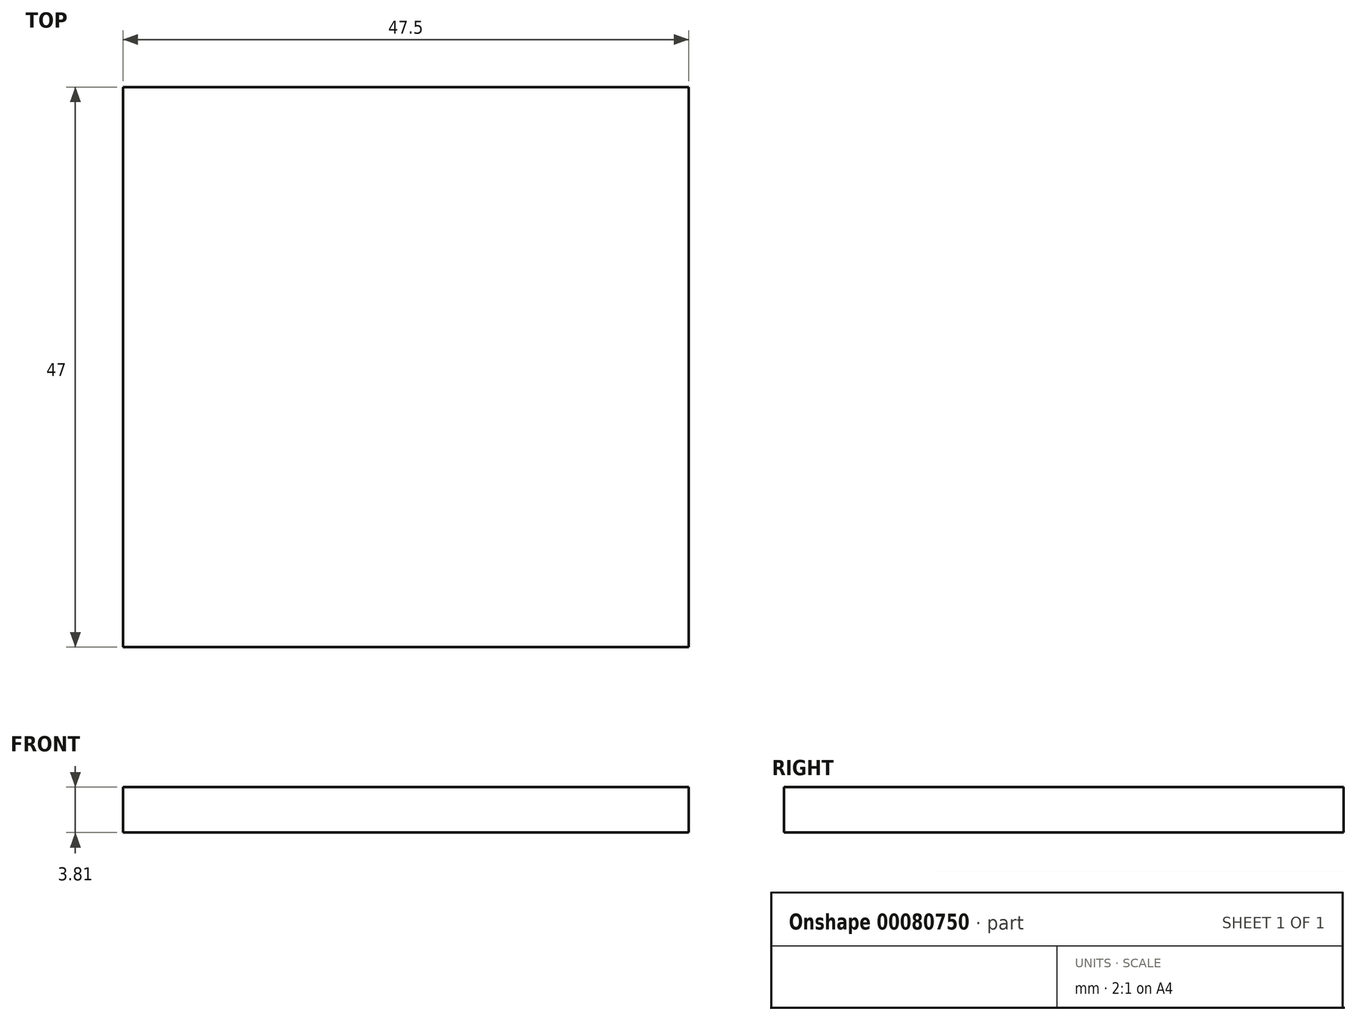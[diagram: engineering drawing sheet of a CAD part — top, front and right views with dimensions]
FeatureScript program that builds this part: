
annotation { "Feature Type Name" : "Feature", "Feature Type Description" : "" }
export const myFeature = defineFeature(function(context is Context, id is Id, definition is map)
    precondition{}
    {
        {
            var Q0;
            Q0=qCreatedBy(makeId("Top.planeOp"),FACE);
            var sketch = newSketch(context, id + "F0", { "sketchPlane" : qUnion([Q0])});
            skLineSegment(sketch, "E0.bottom", {"start": v(23.75, 23.5) * mm, "end": v(-23.75, 23.5) * mm});
            skLineSegment(sketch, "E0.top", {"start": v(23.75, -23.5) * mm, "end": v(-23.75, -23.5) * mm});
            skLineSegment(sketch, "E0.left", {"start": v(23.75, 23.5) * mm, "end": v(23.75, -23.5) * mm});
            skLineSegment(sketch, "E0.right", {"start": v(-23.75, 23.5) * mm, "end": v(-23.75, -23.5) * mm});
            skPoint(sketch, "E0.middle", {"position": v(0, 0) * mm});
            skSolve(sketch);
        }
        {
            var Q0;
            Q0=makeQuery(id+"F0.imprint","IMPRINT",FACE,{"disambiguationData":[TD([[makeQuery(id+"F0.imprint","IMPRINT",EDGE,{"derivedFrom":sQuery(id+"F0.wireOp",EDGE,"E0.bottom")}),1.0]])]});
            extrude(context, id + "F1", {"entities" : qUnion([Q0]), "depth" : 3.8 * mm});
        }
    });
